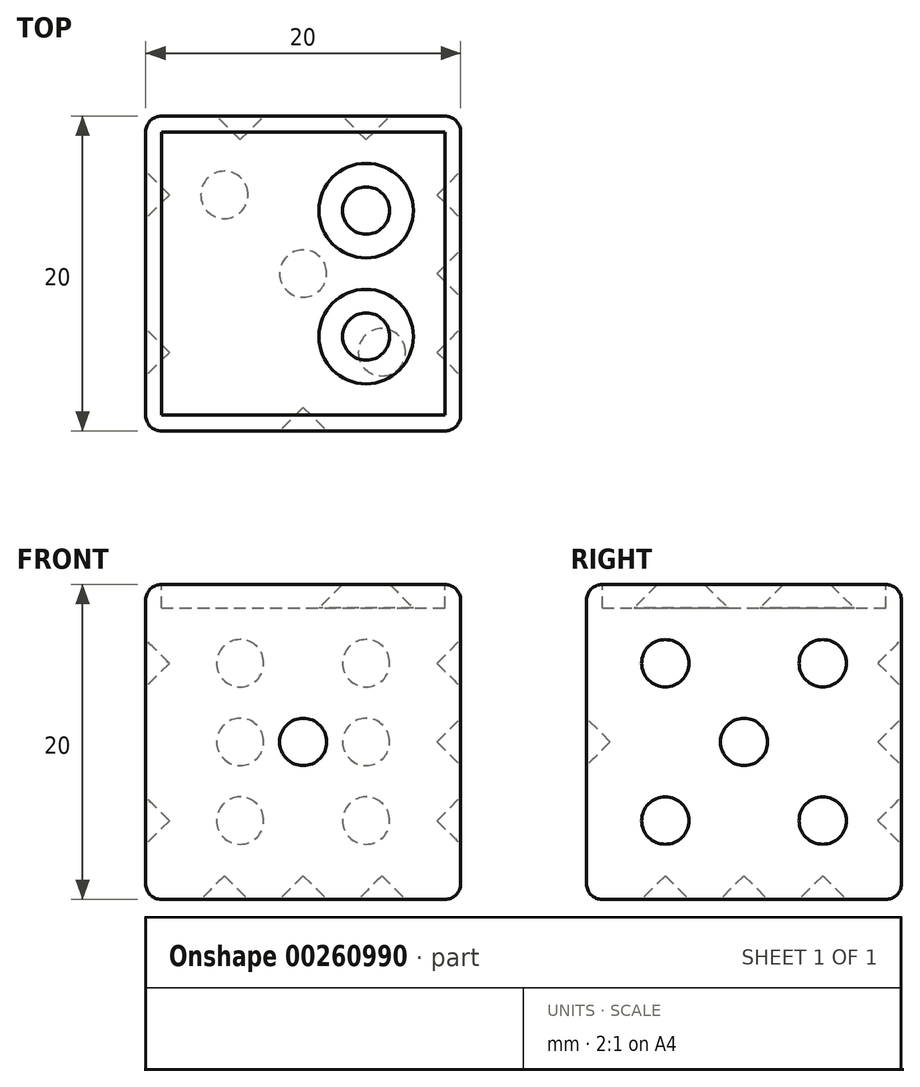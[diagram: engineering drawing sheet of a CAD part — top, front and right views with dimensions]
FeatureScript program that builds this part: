
annotation { "Feature Type Name" : "Feature", "Feature Type Description" : "" }
export const myFeature = defineFeature(function(context is Context, id is Id, definition is map)
    precondition{}
    {
        {
            var Q0;
            Q0=qCreatedBy(makeId("Top.planeOp"),FACE);
            var sketch = newSketch(context, id + "F0", { "sketchPlane" : qUnion([Q0])});
            skLineSegment(sketch, "E0.bottom", {"start": v(0, 0) * mm, "end": v(20, 0) * mm});
            skLineSegment(sketch, "E0.top", {"start": v(0, 20) * mm, "end": v(20, 20) * mm});
            skLineSegment(sketch, "E0.left", {"start": v(0, 0) * mm, "end": v(0, 20) * mm});
            skLineSegment(sketch, "E0.right", {"start": v(20, 0) * mm, "end": v(20, 20) * mm});
            skSolve(sketch);
        }
        {
            var Q0;
            Q0 = qSketchRegion(id + "F0", true);
            extrude(context, id + "F1", {"entities" : qUnion([Q0]), "depth" : 20 * mm});
        }
        {
            var Q0;
            Q0=makeQuery(id+"F1.opExtrude","SWEPT_FACE",FACE,{"disambiguationData":[OSD([sQuery(id+"F0.wireOp",EDGE,"E0.bottom")])]});
            var sketch = newSketch(context, id + "F2", { "sketchPlane" : qUnion([Q0])});
            skLineSegment(sketch, "E1.0", {"start": v(0, 20) * mm, "end": v(20, 20) * mm, "construction": true});
            skLineSegment(sketch, "E1.1", {"start": v(0, 0) * mm, "end": v(20, 0) * mm, "construction": true});
            skLineSegment(sketch, "E2", {"start": v(10, 20) * mm, "end": v(10, 0) * mm, "construction": true});
            skCircle(sketch, "E3", {"center": v(10, 10) * mm, "radius": 1.5 * mm});
            skSolve(sketch);
        }
        {
            var Q0;
            Q0=makeQuery(id+"F2.imprint","IMPRINT",FACE,{"disambiguationData":[TD([[makeQuery(id+"F2.imprint","IMPRINT",EDGE,{"derivedFrom":sQuery(id+"F2.wireOp",EDGE,"E3")}),1.0]])]});
            extrude(context, id + "F3", {"entities" : qUnion([Q0]), "operationType" : NewBodyOperationType.REMOVE, "oppositeDirection" : true, "depth" : 1.5 * mm});
        }
        {
            var Q0;
            Q0=makeQuery(id+"F1.opExtrude","CAP_EDGE",EDGE,{"disambiguationData":[OSD([sQuery(id+"F0.wireOp",EDGE,"E0.left")])],"isStart":false});
            var Q1;
            Q1=makeQuery(id+"F1.opExtrude","SWEPT_EDGE",EDGE,{"disambiguationData":[OSD([sQuery(id+"F0.wireOp",EDGE,"E0.bottom"),sQuery(id+"F0.wireOp",EDGE,"E0.left")])]});
            var Q2;
            Q2=makeQuery(id+"F1.opExtrude","CAP_EDGE",EDGE,{"disambiguationData":[OSD([sQuery(id+"F0.wireOp",EDGE,"E0.bottom")])],"isStart":false});
            var Q3;
            Q3=makeQuery(id+"F1.opExtrude","CAP_EDGE",EDGE,{"disambiguationData":[OSD([sQuery(id+"F0.wireOp",EDGE,"E0.bottom")])],"isStart":true});
            var Q4;
            Q4=makeQuery(id+"F1.opExtrude","SWEPT_EDGE",EDGE,{"disambiguationData":[OSD([sQuery(id+"F0.wireOp",EDGE,"E0.bottom"),sQuery(id+"F0.wireOp",EDGE,"E0.right")])]});
            var Q5;
            Q5=makeQuery(id+"F1.opExtrude","CAP_EDGE",EDGE,{"disambiguationData":[OSD([sQuery(id+"F0.wireOp",EDGE,"E0.right")])],"isStart":false});
            var Q6;
            Q6=makeQuery(id+"F1.opExtrude","SWEPT_EDGE",EDGE,{"disambiguationData":[OSD([sQuery(id+"F0.wireOp",EDGE,"E0.top"),sQuery(id+"F0.wireOp",EDGE,"E0.right")])]});
            var Q7;
            Q7=makeQuery(id+"F1.opExtrude","CAP_EDGE",EDGE,{"disambiguationData":[OSD([sQuery(id+"F0.wireOp",EDGE,"E0.top")])],"isStart":false});
            var Q8;
            Q8=makeQuery(id+"F1.opExtrude","SWEPT_EDGE",EDGE,{"disambiguationData":[OSD([sQuery(id+"F0.wireOp",EDGE,"E0.top"),sQuery(id+"F0.wireOp",EDGE,"E0.left")])]});
            var Q9;
            Q9=makeQuery(id+"F1.opExtrude","CAP_EDGE",EDGE,{"disambiguationData":[OSD([sQuery(id+"F0.wireOp",EDGE,"E0.top")])],"isStart":true});
            var Q10;
            Q10=makeQuery(id+"F1.opExtrude","CAP_EDGE",EDGE,{"disambiguationData":[OSD([sQuery(id+"F0.wireOp",EDGE,"E0.right")])],"isStart":true});
            var Q11;
            Q11=makeQuery(id+"F1.opExtrude","CAP_EDGE",EDGE,{"disambiguationData":[OSD([sQuery(id+"F0.wireOp",EDGE,"E0.left")])],"isStart":true});
            fillet(context, id + "F4", {"entities" : qUnion([Q0, Q1, Q2, Q3, Q4, Q5, Q6, Q7, Q8, Q9, Q10, Q11]), "radius" : 1 * mm, "tangentPropagation" : true, "allowEdgeOverflow" : false});
        }
        {
            var Q0;
            Q0=makeQuery(id+"F1.opExtrude","CAP_FACE",FACE,{"disambiguationData":[OSD([sQuery(id+"F0.wireOp",EDGE,"E0.bottom"),sQuery(id+"F0.wireOp",EDGE,"E0.top"),sQuery(id+"F0.wireOp",EDGE,"E0.left"),sQuery(id+"F0.wireOp",EDGE,"E0.right")])],"isStart":false});
            var sketch = newSketch(context, id + "F5", { "sketchPlane" : qUnion([Q0])});
            skLineSegment(sketch, "E4.0", {"start": v(0, 0) * mm, "end": v(6, 0) * mm, "construction": true});
            skLineSegment(sketch, "E5", {"start": v(6, 20) * mm, "end": v(6, 14) * mm, "construction": true});
            skLineSegment(sketch, "E6", {"start": v(6, 0) * mm, "end": v(6, 6) * mm, "construction": true});
            skCircle(sketch, "E7", {"center": v(6, 14) * mm, "radius": 1.5 * mm});
            skCircle(sketch, "E8", {"center": v(6, 6) * mm, "radius": 1.5 * mm});
            skLineSegment(sketch, "E9", {"start": v(0, 20) * mm, "end": v(6, 20) * mm, "construction": true});
            skLineSegment(sketch, "E10.0", {"start": v(0, 20) * mm, "end": v(20, 20) * mm, "construction": true});
            skLineSegment(sketch, "E10.1", {"start": v(0, 0) * mm, "end": v(20, 0) * mm, "construction": true});
            skLineSegment(sketch, "E11", {"start": v(10, 20) * mm, "end": v(10, 0) * mm, "construction": true});
            skCircle(sketch, "E12.MirrorC", {"center": v(14, 14) * mm, "radius": 1.5 * mm});
            skCircle(sketch, "E13.MirrorC", {"center": v(14, 6) * mm, "radius": 1.5 * mm});
            skSolve(sketch);
        }
        {
            var Q0;
            Q0=makeQuery(id+"F5.imprint","IMPRINT",FACE,{"disambiguationData":[TD([[makeQuery(id+"F5.imprint","IMPRINT",EDGE,{"derivedFrom":sQuery(id+"F5.wireOp",EDGE,"E7")}),1.0]])]});
            var Q1;
            Q1=makeQuery(id+"F5.imprint","IMPRINT",FACE,{"disambiguationData":[TD([[makeQuery(id+"F5.imprint","IMPRINT",EDGE,{"derivedFrom":sQuery(id+"F5.wireOp",EDGE,"E8")}),1.0]])]});
            var Q2;
            Q2=makeQuery(id+"F5.imprint","IMPRINT",FACE,{"disambiguationData":[TD([[makeQuery(id+"F5.imprint","IMPRINT",EDGE,{"derivedFrom":sQuery(id+"F5.wireOp",EDGE,"E13.MirrorC")}),-1.0]])]});
            var Q3;
            Q3=makeQuery(id+"F5.imprint","IMPRINT",FACE,{"disambiguationData":[TD([[makeQuery(id+"F5.imprint","IMPRINT",EDGE,{"derivedFrom":sQuery(id+"F5.wireOp",EDGE,"E12.MirrorC")}),-1.0]])]});
            extrude(context, id + "F6", {"entities" : qUnion([Q0, Q1, Q2, Q3]), "operationType" : NewBodyOperationType.REMOVE, "oppositeDirection" : true, "depth" : 1.5 * mm});
        }
        {
            var Q0;
            Q0=makeQuery(id+"F6.boolean.opBoolean","COPY",EDGE,{"derivedFrom":makeQuery(id+"F6.opExtrude","CAP_EDGE",EDGE,{"disambiguationData":[OSD([sQuery(id+"F5.wireOp",EDGE,"E8")])],"isStart":false})});
            var Q1;
            Q1=makeQuery(id+"F6.boolean.opBoolean","COPY",EDGE,{"derivedFrom":makeQuery(id+"F6.opExtrude","CAP_EDGE",EDGE,{"disambiguationData":[OSD([sQuery(id+"F5.wireOp",EDGE,"E13.MirrorC")])],"isStart":false})});
            var Q2;
            Q2=makeQuery(id+"F6.boolean.opBoolean","COPY",EDGE,{"derivedFrom":makeQuery(id+"F6.opExtrude","CAP_EDGE",EDGE,{"disambiguationData":[OSD([sQuery(id+"F5.wireOp",EDGE,"E12.MirrorC")])],"isStart":false})});
            var Q3;
            Q3=makeQuery(id+"F6.boolean.opBoolean","COPY",EDGE,{"derivedFrom":makeQuery(id+"F6.opExtrude","CAP_EDGE",EDGE,{"disambiguationData":[OSD([sQuery(id+"F5.wireOp",EDGE,"E7")])],"isStart":false})});
            var Q4;
            Q4=makeQuery(id+"F3.boolean.opBoolean","COPY",FACE,{"derivedFrom":makeQuery(id+"F3.opExtrude","CAP_FACE",FACE,{"disambiguationData":[OSD([sQuery(id+"F2.wireOp",EDGE,"E3")])],"isStart":false})});
            chamfer(context, id + "F7", {"entities" : qUnion([Q0, Q1, Q2, Q3, Q4]), "width" : 1.5 * mm, "tangentPropagation" : true});
        }
        {
            var Q0;
            Q0=makeQuery(id+"F1.opExtrude","SWEPT_FACE",FACE,{"disambiguationData":[OSD([sQuery(id+"F0.wireOp",EDGE,"E0.right")])]});
            var sketch = newSketch(context, id + "F8", { "sketchPlane" : qUnion([Q0])});
            skLineSegment(sketch, "E14.0", {"start": v(0, 20) * mm, "end": v(20, 20) * mm});
            skLineSegment(sketch, "E15.0", {"start": v(0, 0) * mm, "end": v(20, 0) * mm});
            skLineSegment(sketch, "E16", {"start": v(0, 20) * mm, "end": v(10, 20) * mm});
            skLineSegment(sketch, "E17", {"start": v(10, 0) * mm, "end": v(5, 0) * mm, "construction": true});
            skLineSegment(sketch, "E18", {"start": v(10, 0) * mm, "end": v(15, 0) * mm});
            skLineSegment(sketch, "E19", {"start": v(10, 0) * mm, "end": v(15, 0) * mm, "construction": true});
            skLineSegment(sketch, "E20", {"start": v(10, 20) * mm, "end": v(15, 20) * mm, "construction": true});
            skLineSegment(sketch, "E21", {"start": v(10, 20) * mm, "end": v(5, 20) * mm, "construction": true});
            skLineSegment(sketch, "E22", {"start": v(0, 10) * mm, "end": v(0, 15) * mm, "construction": true});
            skLineSegment(sketch, "E23", {"start": v(20, 10) * mm, "end": v(20, 15) * mm});
            skLineSegment(sketch, "E24", {"start": v(20, 10) * mm, "end": v(20, 5) * mm});
            skLineSegment(sketch, "E25", {"start": v(0, 10) * mm, "end": v(0, 5) * mm});
            skCircle(sketch, "E26", {"center": v(10, 10) * mm, "radius": 1.5 * mm});
            skCircle(sketch, "E27", {"center": v(5, 15) * mm, "radius": 1.5 * mm});
            skCircle(sketch, "E28", {"center": v(15, 15) * mm, "radius": 1.5 * mm});
            skCircle(sketch, "E29", {"center": v(15, 5) * mm, "radius": 1.5 * mm});
            skCircle(sketch, "E30", {"center": v(5, 5) * mm, "radius": 1.5 * mm});
            skSolve(sketch);
        }
        {
            var Q0;
            Q0=makeQuery(id+"F8.imprint","IMPRINT",FACE,{"disambiguationData":[TD([[makeQuery(id+"F8.imprint","IMPRINT",EDGE,{"derivedFrom":sQuery(id+"F8.wireOp",EDGE,"E26")}),1.0]])]});
            var Q1;
            Q1=makeQuery(id+"F8.imprint","IMPRINT",FACE,{"disambiguationData":[TD([[makeQuery(id+"F8.imprint","IMPRINT",EDGE,{"derivedFrom":sQuery(id+"F8.wireOp",EDGE,"E29")}),1.0]])]});
            var Q2;
            Q2=makeQuery(id+"F8.imprint","IMPRINT",FACE,{"disambiguationData":[TD([[makeQuery(id+"F8.imprint","IMPRINT",EDGE,{"derivedFrom":sQuery(id+"F8.wireOp",EDGE,"E28")}),1.0]])]});
            var Q3;
            Q3=makeQuery(id+"F8.imprint","IMPRINT",FACE,{"disambiguationData":[TD([[makeQuery(id+"F8.imprint","IMPRINT",EDGE,{"derivedFrom":sQuery(id+"F8.wireOp",EDGE,"E27")}),1.0]])]});
            var Q4;
            Q4=makeQuery(id+"F8.imprint","IMPRINT",FACE,{"disambiguationData":[TD([[makeQuery(id+"F8.imprint","IMPRINT",EDGE,{"derivedFrom":sQuery(id+"F8.wireOp",EDGE,"E30")}),1.0]])]});
            extrude(context, id + "F9", {"entities" : qUnion([Q0, Q1, Q2, Q3, Q4]), "operationType" : NewBodyOperationType.REMOVE, "oppositeDirection" : true, "depth" : 1.5 * mm});
        }
        {
            var Q0;
            Q0=makeQuery(id+"F9.boolean.opBoolean","COPY",EDGE,{"derivedFrom":makeQuery(id+"F9.opExtrude","CAP_EDGE",EDGE,{"disambiguationData":[OSD([sQuery(id+"F8.wireOp",EDGE,"E27")])],"isStart":false})});
            var Q1;
            Q1=makeQuery(id+"F9.boolean.opBoolean","COPY",EDGE,{"derivedFrom":makeQuery(id+"F9.opExtrude","CAP_EDGE",EDGE,{"disambiguationData":[OSD([sQuery(id+"F8.wireOp",EDGE,"E30")])],"isStart":false})});
            var Q2;
            Q2=makeQuery(id+"F9.boolean.opBoolean","COPY",EDGE,{"derivedFrom":makeQuery(id+"F9.opExtrude","CAP_EDGE",EDGE,{"disambiguationData":[OSD([sQuery(id+"F8.wireOp",EDGE,"E26")])],"isStart":false})});
            var Q3;
            Q3=makeQuery(id+"F9.boolean.opBoolean","COPY",EDGE,{"derivedFrom":makeQuery(id+"F9.opExtrude","CAP_EDGE",EDGE,{"disambiguationData":[OSD([sQuery(id+"F8.wireOp",EDGE,"E28")])],"isStart":false})});
            var Q4;
            Q4=makeQuery(id+"F9.boolean.opBoolean","COPY",EDGE,{"derivedFrom":makeQuery(id+"F9.opExtrude","CAP_EDGE",EDGE,{"disambiguationData":[OSD([sQuery(id+"F8.wireOp",EDGE,"E29")])],"isStart":false})});
            chamfer(context, id + "F10", {"entities" : qUnion([Q0, Q1, Q2, Q3, Q4]), "width" : 1.5 * mm, "tangentPropagation" : true});
        }
        {
            var Q0;
            Q0=makeQuery(id+"F1.opExtrude","SWEPT_FACE",FACE,{"disambiguationData":[OSD([sQuery(id+"F0.wireOp",EDGE,"E0.top")])]});
            var sketch = newSketch(context, id + "F11", { "sketchPlane" : qUnion([Q0])});
            skPoint(sketch, "E31.0", {"position": v(-20, 15) * mm});
            skPoint(sketch, "E31.1", {"position": v(-20, 10) * mm});
            skPoint(sketch, "E31.2", {"position": v(-20, 5) * mm});
            skLineSegment(sketch, "E31.3", {"start": v(0, 0) * mm, "end": v(-20, 0) * mm});
            skLineSegment(sketch, "E31.4", {"start": v(0, 20) * mm, "end": v(0, 0) * mm});
            skLineSegment(sketch, "E31.5", {"start": v(0, 20) * mm, "end": v(-20, 20) * mm});
            skLineSegment(sketch, "E32", {"start": v(-20, 20) * mm, "end": v(-14, 20) * mm});
            skLineSegment(sketch, "E33", {"start": v(0, 20) * mm, "end": v(-6, 20) * mm});
            skLineSegment(sketch, "E34", {"start": v(-20, 0) * mm, "end": v(-14, 0) * mm});
            skLineSegment(sketch, "E35", {"start": v(0, 0) * mm, "end": v(-6, 0) * mm});
            skCircle(sketch, "E36", {"center": v(-14, 15) * mm, "radius": 1.5 * mm});
            skCircle(sketch, "E37", {"center": v(-14, 10) * mm, "radius": 1.5 * mm});
            skCircle(sketch, "E38", {"center": v(-14, 5) * mm, "radius": 1.5 * mm});
            skCircle(sketch, "E39", {"center": v(-6, 10) * mm, "radius": 1.5 * mm});
            skCircle(sketch, "E40", {"center": v(-6, 5) * mm, "radius": 1.5 * mm});
            skCircle(sketch, "E41", {"center": v(-6, 15) * mm, "radius": 1.5 * mm});
            skSolve(sketch);
        }
        {
            var Q0;
            Q0=makeQuery(id+"F11.imprint","IMPRINT",FACE,{"disambiguationData":[TD([[makeQuery(id+"F11.imprint","IMPRINT",EDGE,{"derivedFrom":sQuery(id+"F11.wireOp",EDGE,"E36")}),1.0]])]});
            var Q1;
            Q1=makeQuery(id+"F11.imprint","IMPRINT",FACE,{"disambiguationData":[TD([[makeQuery(id+"F11.imprint","IMPRINT",EDGE,{"derivedFrom":sQuery(id+"F11.wireOp",EDGE,"E37")}),1.0]])]});
            var Q2;
            Q2=makeQuery(id+"F11.imprint","IMPRINT",FACE,{"disambiguationData":[TD([[makeQuery(id+"F11.imprint","IMPRINT",EDGE,{"derivedFrom":sQuery(id+"F11.wireOp",EDGE,"E38")}),1.0]])]});
            var Q3;
            Q3=makeQuery(id+"F11.imprint","IMPRINT",FACE,{"disambiguationData":[TD([[makeQuery(id+"F11.imprint","IMPRINT",EDGE,{"derivedFrom":sQuery(id+"F11.wireOp",EDGE,"E40")}),1.0]])]});
            var Q4;
            Q4=makeQuery(id+"F11.imprint","IMPRINT",FACE,{"disambiguationData":[TD([[makeQuery(id+"F11.imprint","IMPRINT",EDGE,{"derivedFrom":sQuery(id+"F11.wireOp",EDGE,"E39")}),1.0]])]});
            var Q5;
            Q5=makeQuery(id+"F11.imprint","IMPRINT",FACE,{"disambiguationData":[TD([[makeQuery(id+"F11.imprint","IMPRINT",EDGE,{"derivedFrom":sQuery(id+"F11.wireOp",EDGE,"E41")}),1.0]])]});
            extrude(context, id + "F12", {"entities" : qUnion([Q0, Q1, Q2, Q3, Q4, Q5]), "operationType" : NewBodyOperationType.REMOVE, "oppositeDirection" : true, "depth" : 1.5 * mm});
        }
        {
            var Q0;
            Q0=makeQuery(id+"F12.boolean.opBoolean","COPY",FACE,{"derivedFrom":makeQuery(id+"F12.opExtrude","CAP_FACE",FACE,{"disambiguationData":[OSD([sQuery(id+"F11.wireOp",EDGE,"E36")])],"isStart":false})});
            var Q1;
            Q1=makeQuery(id+"F12.boolean.opBoolean","COPY",EDGE,{"derivedFrom":makeQuery(id+"F12.opExtrude","CAP_EDGE",EDGE,{"disambiguationData":[OSD([sQuery(id+"F11.wireOp",EDGE,"E41")])],"isStart":false})});
            var Q2;
            Q2=makeQuery(id+"F12.boolean.opBoolean","COPY",EDGE,{"derivedFrom":makeQuery(id+"F12.opExtrude","CAP_EDGE",EDGE,{"disambiguationData":[OSD([sQuery(id+"F11.wireOp",EDGE,"E39")])],"isStart":false})});
            var Q3;
            Q3=makeQuery(id+"F12.boolean.opBoolean","COPY",EDGE,{"derivedFrom":makeQuery(id+"F12.opExtrude","CAP_EDGE",EDGE,{"disambiguationData":[OSD([sQuery(id+"F11.wireOp",EDGE,"E37")])],"isStart":false})});
            var Q4;
            Q4=makeQuery(id+"F12.boolean.opBoolean","COPY",FACE,{"derivedFrom":makeQuery(id+"F12.opExtrude","CAP_FACE",FACE,{"disambiguationData":[OSD([sQuery(id+"F11.wireOp",EDGE,"E38")])],"isStart":false})});
            var Q5;
            Q5=makeQuery(id+"F12.boolean.opBoolean","COPY",FACE,{"derivedFrom":makeQuery(id+"F12.opExtrude","CAP_FACE",FACE,{"disambiguationData":[OSD([sQuery(id+"F11.wireOp",EDGE,"E40")])],"isStart":false})});
            chamfer(context, id + "F13", {"entities" : qUnion([Q0, Q1, Q2, Q3, Q4, Q5]), "width" : 1.5 * mm, "tangentPropagation" : true});
        }
        {
            var Q0;
            Q0=makeQuery(id+"F1.opExtrude","CAP_FACE",FACE,{"disambiguationData":[OSD([sQuery(id+"F0.wireOp",EDGE,"E0.bottom"),sQuery(id+"F0.wireOp",EDGE,"E0.top"),sQuery(id+"F0.wireOp",EDGE,"E0.left"),sQuery(id+"F0.wireOp",EDGE,"E0.right")])],"isStart":true});
            var sketch = newSketch(context, id + "F14", { "sketchPlane" : qUnion([Q0])});
            skLineSegment(sketch, "E42.0", {"start": v(0, 0) * mm, "end": v(20, 0) * mm});
            skLineSegment(sketch, "E42.1", {"start": v(0, 0) * mm, "end": v(0, -20) * mm});
            skLineSegment(sketch, "E42.2", {"start": v(0, -20) * mm, "end": v(20, -20) * mm});
            skLineSegment(sketch, "E42.3", {"start": v(20, 0) * mm, "end": v(20, -20) * mm});
            skPoint(sketch, "E43.0", {"position": v(20, -5) * mm});
            skPoint(sketch, "E43.1", {"position": v(20, -10) * mm});
            skPoint(sketch, "E43.2", {"position": v(20, -15) * mm});
            skLineSegment(sketch, "E44", {"start": v(20, -5) * mm, "end": v(0, -5) * mm, "construction": true});
            skLineSegment(sketch, "E45", {"start": v(20, -10) * mm, "end": v(0, -10) * mm, "construction": true});
            skLineSegment(sketch, "E46", {"start": v(20, -15) * mm, "end": v(0, -15) * mm, "construction": true});
            skLineSegment(sketch, "E47", {"start": v(10, -20) * mm, "end": v(5, -20) * mm});
            skLineSegment(sketch, "E48", {"start": v(10, -20) * mm, "end": v(15, -20) * mm});
            skLineSegment(sketch, "E49", {"start": v(5, -20) * mm, "end": v(5, 0) * mm, "construction": true});
            skLineSegment(sketch, "E50", {"start": v(10, -20) * mm, "end": v(10, 0) * mm, "construction": true});
            skLineSegment(sketch, "E51", {"start": v(15, -20) * mm, "end": v(15, 0) * mm, "construction": true});
            skCircle(sketch, "E52", {"center": v(5, -15) * mm, "radius": 1.5 * mm});
            skCircle(sketch, "E53", {"center": v(10, -10) * mm, "radius": 1.5 * mm});
            skCircle(sketch, "E54", {"center": v(15, -5) * mm, "radius": 1.5 * mm});
            skSolve(sketch);
        }
        {
            var Q0;
            Q0=makeQuery(id+"F1.opExtrude","SWEPT_FACE",FACE,{"disambiguationData":[OSD([sQuery(id+"F0.wireOp",EDGE,"E0.left")])]});
            var sketch = newSketch(context, id + "F15", { "sketchPlane" : qUnion([Q0])});
            skPoint(sketch, "E55.0", {"position": v(-5, 15) * mm});
            skPoint(sketch, "E55.1", {"position": v(-15, 5) * mm});
            skCircle(sketch, "E55.2", {"center": v(-5, 15) * mm, "radius": 1.5 * mm, "construction": true});
            skCircle(sketch, "E55.3", {"center": v(-15, 5) * mm, "radius": 1.5 * mm, "construction": true});
            skCircle(sketch, "E56", {"center": v(-5, 15) * mm, "radius": 1.5 * mm});
            skCircle(sketch, "E57", {"center": v(-15, 5) * mm, "radius": 1.5 * mm});
            skSolve(sketch);
        }
        {
            var Q0;
            Q0=makeQuery(id+"F15.imprint","IMPRINT",FACE,{"disambiguationData":[TD([[makeQuery(id+"F15.imprint","IMPRINT",EDGE,{"derivedFrom":sQuery(id+"F15.wireOp",EDGE,"E57")}),1.0]])]});
            var Q1;
            Q1=makeQuery(id+"F15.imprint","IMPRINT",FACE,{"disambiguationData":[TD([[makeQuery(id+"F15.imprint","IMPRINT",EDGE,{"derivedFrom":sQuery(id+"F15.wireOp",EDGE,"E56")}),1.0]])]});
            extrude(context, id + "F16", {"entities" : qUnion([Q0, Q1]), "operationType" : NewBodyOperationType.REMOVE, "oppositeDirection" : true, "depth" : 1.5 * mm});
        }
        {
            var Q0;
            Q0=makeQuery(id+"F16.boolean.opBoolean","COPY",FACE,{"derivedFrom":makeQuery(id+"F16.opExtrude","CAP_FACE",FACE,{"disambiguationData":[OSD([sQuery(id+"F15.wireOp",EDGE,"E57")])],"isStart":false})});
            var Q1;
            Q1=makeQuery(id+"F16.boolean.opBoolean","COPY",FACE,{"derivedFrom":makeQuery(id+"F16.opExtrude","CAP_FACE",FACE,{"disambiguationData":[OSD([sQuery(id+"F15.wireOp",EDGE,"E56")])],"isStart":false})});
            chamfer(context, id + "F17", {"entities" : qUnion([Q0, Q1]), "width" : 1.5 * mm, "tangentPropagation" : true});
        }
        {
            var Q0;
            Q0=makeQuery(id+"F14.imprint","IMPRINT",FACE,{"disambiguationData":[TD([[makeQuery(id+"F14.imprint","IMPRINT",EDGE,{"derivedFrom":sQuery(id+"F14.wireOp",EDGE,"E52")}),1.0]])]});
            var Q1;
            Q1=makeQuery(id+"F14.imprint","IMPRINT",FACE,{"disambiguationData":[TD([[makeQuery(id+"F14.imprint","IMPRINT",EDGE,{"derivedFrom":sQuery(id+"F14.wireOp",EDGE,"E53")}),1.0]])]});
            var Q2;
            Q2=makeQuery(id+"F14.imprint","IMPRINT",FACE,{"disambiguationData":[TD([[makeQuery(id+"F14.imprint","IMPRINT",EDGE,{"derivedFrom":sQuery(id+"F14.wireOp",EDGE,"E54")}),1.0]])]});
            extrude(context, id + "F18", {"entities" : qUnion([Q0, Q1, Q2]), "operationType" : NewBodyOperationType.REMOVE, "oppositeDirection" : true, "depth" : 1.5 * mm});
        }
        {
            var Q0;
            Q0=makeQuery(id+"F18.boolean.opBoolean","COPY",FACE,{"derivedFrom":makeQuery(id+"F18.opExtrude","CAP_FACE",FACE,{"disambiguationData":[OSD([sQuery(id+"F14.wireOp",EDGE,"E54")])],"isStart":false})});
            var Q1;
            Q1=makeQuery(id+"F18.boolean.opBoolean","COPY",FACE,{"derivedFrom":makeQuery(id+"F18.opExtrude","CAP_FACE",FACE,{"disambiguationData":[OSD([sQuery(id+"F14.wireOp",EDGE,"E53")])],"isStart":false})});
            var Q2;
            Q2=makeQuery(id+"F18.boolean.opBoolean","COPY",FACE,{"derivedFrom":makeQuery(id+"F18.opExtrude","CAP_FACE",FACE,{"disambiguationData":[OSD([sQuery(id+"F14.wireOp",EDGE,"E52")])],"isStart":false})});
            chamfer(context, id + "F19", {"entities" : qUnion([Q0, Q1, Q2]), "width" : 1.5 * mm, "tangentPropagation" : true});
        }
    });
